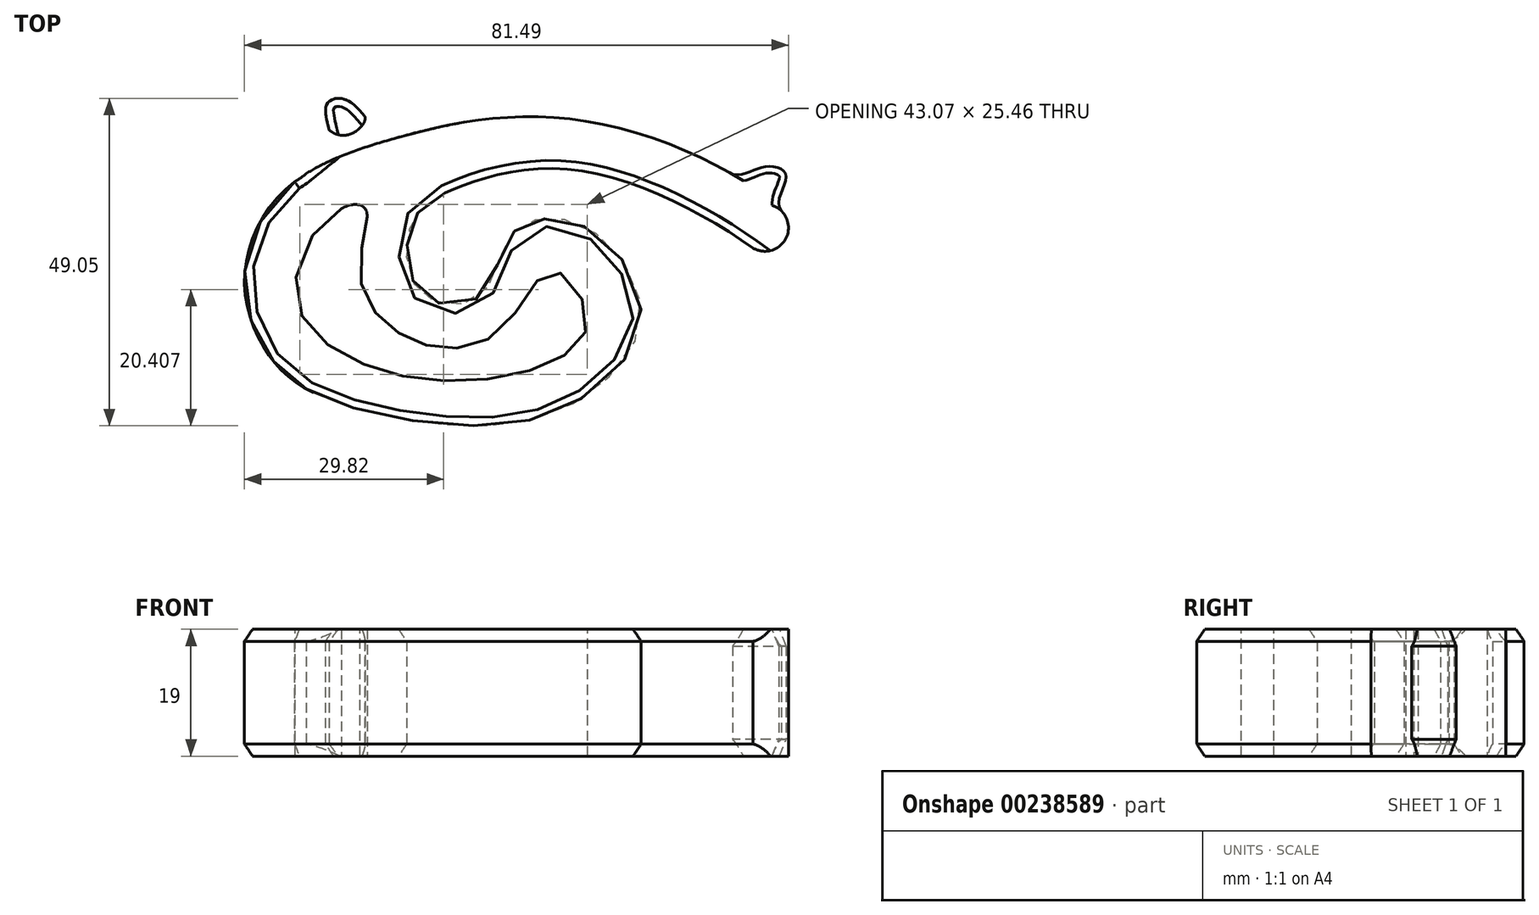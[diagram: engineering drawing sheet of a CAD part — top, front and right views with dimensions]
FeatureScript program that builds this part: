
annotation { "Feature Type Name" : "Feature", "Feature Type Description" : "" }
export const myFeature = defineFeature(function(context is Context, id is Id, definition is map)
    precondition{}
    {
        {
            var Q0;
            Q0=qCreatedBy(makeId("Top.planeOp"),FACE);
            var sketch = newSketch(context, id + "F0", { "sketchPlane" : qUnion([Q0])});
            skFitSpline(sketch, "E0", {"points": [v(27.49, 43.05) * mm, v(-2.7, 56.63) * mm, v(-30.14, 53.98) * mm, v(-46.98, 46.08) * mm, v(-52.93, 32.92) * mm, v(-49, 21.03) * mm, v(-40.31, 14.78) * mm, v(-21, 10.95) * mm, v(-4.09, 14) * mm, v(6.45, 26.76) * mm, v(-0.2, 39.64) * mm, v(-8.98, 41.74) * mm, v(-13.65, 38.45) * mm, v(-17.62, 30.29) * mm, v(-24.92, 29.63) * mm, v(-28.47, 35) * mm, v(-27.55, 41.89) * mm, v(-22.9, 45.7) * mm, v(-4.02, 49.25) * mm, v(23.22, 37.5) * mm], "startDerivative": vector(-229.6, 231) * mm, "endDerivative": vector(281.68, -199.14) * mm});
            skFitSpline(sketch, "E1", {"points": [v(-38.39, 43.39) * mm, v(-45.3, 30.53) * mm, v(-36.9, 20.89) * mm, v(-22.23, 17.55) * mm, v(-6.84, 20.43) * mm, v(-1.55, 26.92) * mm, v(-6.78, 34.05) * mm, v(-13.85, 25.9) * mm, v(-22.75, 22.45) * mm, v(-30.37, 25.1) * mm, v(-35.4, 32.15) * mm, v(-34.54, 42.2) * mm], "startDerivative": vector(-108.7, -45.07) * mm, "endDerivative": vector(13.61, 86.54) * mm});
            skFitSpline(sketch, "E2", {"points": [v(-38.39, 43.39) * mm, v(-34.54, 42.2) * mm], "startDerivative": vector(5.06, 2.98) * mm, "endDerivative": vector(-0.21, -6.41) * mm});
            skLineSegment(sketch, "E3", {"start": v(-30.14, 53.98) * mm, "end": v(-22.9, 45.7) * mm});
            skArc(sketch, "E4", {"start": v(23.22, 37.5) * mm, "mid": v(27.83, 38.37) * mm, "end": v(27.49, 43.05) * mm});
            skFitSpline(sketch, "E5", {"points": [v(27.49, 43.05) * mm, v(28.21, 48.3) * mm, v(25.15, 49.7) * mm, v(20.2, 48.52) * mm], "startDerivative": vector(-10.45, 12.75) * mm, "endDerivative": vector(-17.8, 2.48) * mm});
            skFitSpline(sketch, "E6", {"points": [v(-30.51, 53.88) * mm, v(-33.88, 55.91) * mm, v(-37.96, 59.77) * mm, v(-40.66, 58.89) * mm, v(-40.12, 54.24) * mm, v(-41.06, 51.41) * mm, v(-45.4, 47.43) * mm], "startDerivative": vector(-33.71, 1.53) * mm, "endDerivative": vector(-31.88, -18.97) * mm});
            skFitSpline(sketch, "E7", {"points": [v(-40.27, 55.18) * mm, v(-36.79, 54.67) * mm, v(-34.92, 57.24) * mm], "startDerivative": vector(6.06, -5.1) * mm, "endDerivative": vector(-2.07, 5.05) * mm});
            skSolve(sketch);
        }
        {
            var Q0;
            Q0=makeQuery(id+"F0.imprint","IMPRINT",FACE,{"disambiguationData":[TD([[makeQuery(id+"F0.imprint","IMPRINT",EDGE,{"derivedFrom":sQuery(id+"F0.wireOp",EDGE,"E1")}),-1.0]])]});
            var Q1;
            {var subQ2=sQuery(id+"F0.wireOp",EDGE,"E3");Q1=makeQuery(id+"F0.imprint","IMPRINT",FACE,{"disambiguationData":[TD([[makeQuery(id+"F0.imprint","IMPRINT",EDGE,{"derivedFrom":subQ2}),1.0]])]});}
            var Q2;
            {var subQ0=sQuery(id+"F0.wireOp",EDGE,"E5");Q2=makeQuery(id+"F0.imprint","IMPRINT",FACE,{"disambiguationData":[TD([[makeQuery(id+"F0.imprint","IMPRINT",EDGE,{"derivedFrom":subQ0}),1.0]])]});}
            var Q3;
            {var subQ0=sQuery(id+"F0.wireOp",EDGE,"eccfb569-30d1-4c66-bf5a-0c2657435a2f");var subQ1=sQuery(id+"F0.wireOp",EDGE,"E0");var subQ3=makeQuery(id+"F0.imprint","INTERSECT",VERTEX,{"disambiguationData":[OD(1.0)],"derivedFrom":[subQ1,subQ0]});Q3=makeQuery(id+"F0.imprint","IMPRINT",FACE,{"disambiguationData":[TD([[makeQuery(id+"F0.imprint","IMPRINT",EDGE,{"disambiguationData":[TD([[subQ3,1.0]])],"derivedFrom":subQ1}),-1.0]])]});}
            var Q4;
            {var subQ0=sQuery(id+"F0.wireOp",EDGE,"E6");var subQ1=sQuery(id+"F0.wireOp",EDGE,"E0");var subQ2=makeQuery(id+"F0.imprint","INTERSECT",VERTEX,{"disambiguationData":[OD(0.0)],"derivedFrom":[subQ1,subQ0]});Q4=makeQuery(id+"F0.imprint","IMPRINT",FACE,{"disambiguationData":[TD([[makeQuery(id+"F0.imprint","IMPRINT",EDGE,{"disambiguationData":[TD([[subQ2,-1.0]])],"derivedFrom":subQ1}),-1.0]])]});}
            var Q5;
            {var subQ0=sQuery(id+"F0.wireOp",EDGE,"E7");Q5=makeQuery(id+"F0.imprint","IMPRINT",FACE,{"disambiguationData":[TD([[makeQuery(id+"F0.imprint","IMPRINT",EDGE,{"derivedFrom":subQ0}),1.0]])]});}
            extrude(context, id + "F1", {"entities" : qUnion([Q0, Q1, Q2, Q3, Q4, Q5]), "flatOperationType" : FlatOperationType.REMOVE, "offsetDistance" : 25 * mm, "depth" : 19 * mm, "hasSecondDirection" : true, "secondDirectionOppositeDirection" : true, "secondDirectionDepth" : 12.5 * mm, "domain" : OperationDomain.MODEL, "symmetric" : true});
        }
        {
            var Q0;
            {var subQ0=sQuery(id+"F0.wireOp",EDGE,"E0");var subQ1=makeQuery(id+"F0.imprint","INTERSECT",VERTEX,{"disambiguationData":[OD(1.0)],"derivedFrom":[subQ0,sQuery(id+"F0.wireOp",EDGE,"E3")]});Q0=makeQuery(id+"F1.opExtrude","CAP_EDGE",EDGE,{"disambiguationData":[OSD([subQ0]),TDD([makeQuery(id+"F0.imprint","IMPRINT",EDGE,{"disambiguationData":[TD([[subQ1,1.0]])],"derivedFrom":subQ0}),makeQuery(id+"F0.imprint","IMPRINT",EDGE,{"disambiguationData":[TD([[makeQuery(id+"F0.imprint","INTERSECT",VERTEX,{"derivedFrom":[subQ0,sQuery(id+"F0.wireOp",EDGE,"E4")]}),1.0]])],"derivedFrom":subQ0})])],"isStart":false});}
            var Q1;
            Q1=makeQuery(id+"F1.opExtrude","CAP_EDGE",EDGE,{"disambiguationData":[OSD([sQuery(id+"F0.wireOp",EDGE,"E6")])],"isStart":false});
            chamfer(context, id + "F2", {"entities" : qUnion([Q0, Q1]), "chamferType" : ChamferType.TWO_OFFSETS, "width1" : 1.8 * mm, "oppositeDirection" : true, "width2" : 1.2 * mm, "tangentPropagation" : true});
        }
        {
            var Q0;
            {var subQ0=sQuery(id+"F0.wireOp",EDGE,"E0");var subQ1=makeQuery(id+"F0.imprint","INTERSECT",VERTEX,{"disambiguationData":[OD(1.0)],"derivedFrom":[subQ0,sQuery(id+"F0.wireOp",EDGE,"E3")]});Q0=makeQuery(id+"F1.opExtrude","CAP_EDGE",EDGE,{"disambiguationData":[OSD([subQ0]),TDD([makeQuery(id+"F0.imprint","IMPRINT",EDGE,{"disambiguationData":[TD([[subQ1,1.0]])],"derivedFrom":subQ0}),makeQuery(id+"F0.imprint","IMPRINT",EDGE,{"disambiguationData":[TD([[makeQuery(id+"F0.imprint","INTERSECT",VERTEX,{"derivedFrom":[subQ0,sQuery(id+"F0.wireOp",EDGE,"E4")]}),1.0]])],"derivedFrom":subQ0})])],"isStart":true});}
            var Q1;
            Q1=makeQuery(id+"F1.opExtrude","CAP_EDGE",EDGE,{"disambiguationData":[OSD([sQuery(id+"F0.wireOp",EDGE,"E6")])],"isStart":true});
            chamfer(context, id + "F3", {"entities" : qUnion([Q0, Q1]), "chamferType" : ChamferType.TWO_OFFSETS, "width1" : 1.2 * mm, "oppositeDirection" : true, "width2" : 1.8 * mm, "tangentPropagation" : true});
        }
        {
            var Q0;
            Q0=makeQuery(id+"F1.opExtrude","CAP_EDGE",EDGE,{"disambiguationData":[OSD([sQuery(id+"F0.wireOp",EDGE,"E5")])],"isStart":false});
            var Q1;
            Q1=makeQuery(id+"F1.opExtrude","CAP_EDGE",EDGE,{"disambiguationData":[OSD([sQuery(id+"F0.wireOp",EDGE,"E5")])],"isStart":true});
            chamfer(context, id + "F4", {"entities" : qUnion([Q0, Q1]), "chamferType" : ChamferType.TWO_OFFSETS, "width1" : 1 * mm, "oppositeDirection" : false, "width2" : 2.5 * mm, "tangentPropagation" : true});
        }
    });
